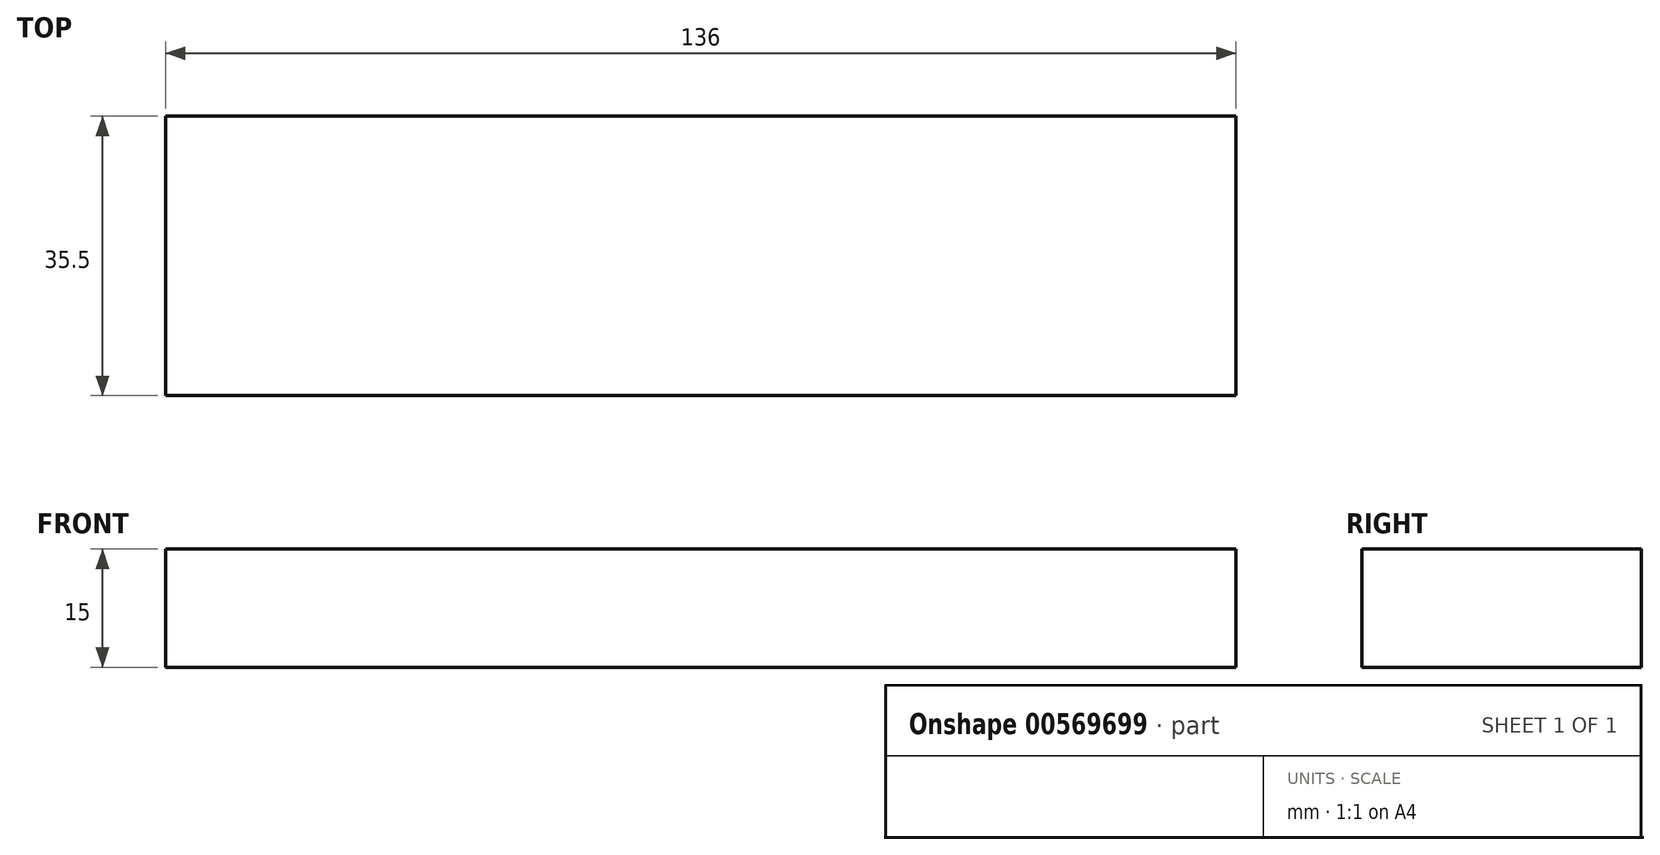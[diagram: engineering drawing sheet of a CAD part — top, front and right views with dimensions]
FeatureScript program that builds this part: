
annotation { "Feature Type Name" : "Feature", "Feature Type Description" : "" }
export const myFeature = defineFeature(function(context is Context, id is Id, definition is map)
    precondition{}
    {
        {
            var Q0;
            Q0=qCreatedBy(makeId("Top.planeOp"),FACE);
            var sketch = newSketch(context, id + "F0", { "sketchPlane" : qUnion([Q0])});
            skLineSegment(sketch, "E0.bottom", {"start": v(-82.5, 20.5) * mm, "end": v(53.5, 20.5) * mm});
            skLineSegment(sketch, "E0.top", {"start": v(-82.5, -15) * mm, "end": v(53.5, -15) * mm});
            skLineSegment(sketch, "E0.left", {"start": v(-82.5, 20.5) * mm, "end": v(-82.5, -15) * mm});
            skLineSegment(sketch, "E0.right", {"start": v(53.5, 20.5) * mm, "end": v(53.5, -15) * mm});
            skSolve(sketch);
        }
        {
            var Q0;
            Q0 = qSketchRegion(id + "F0", true);
            extrude(context, id + "F1", {"entities" : qUnion([Q0]), "depth" : 15 * mm, "offsetDistance" : 25 * mm});
        }
    });
